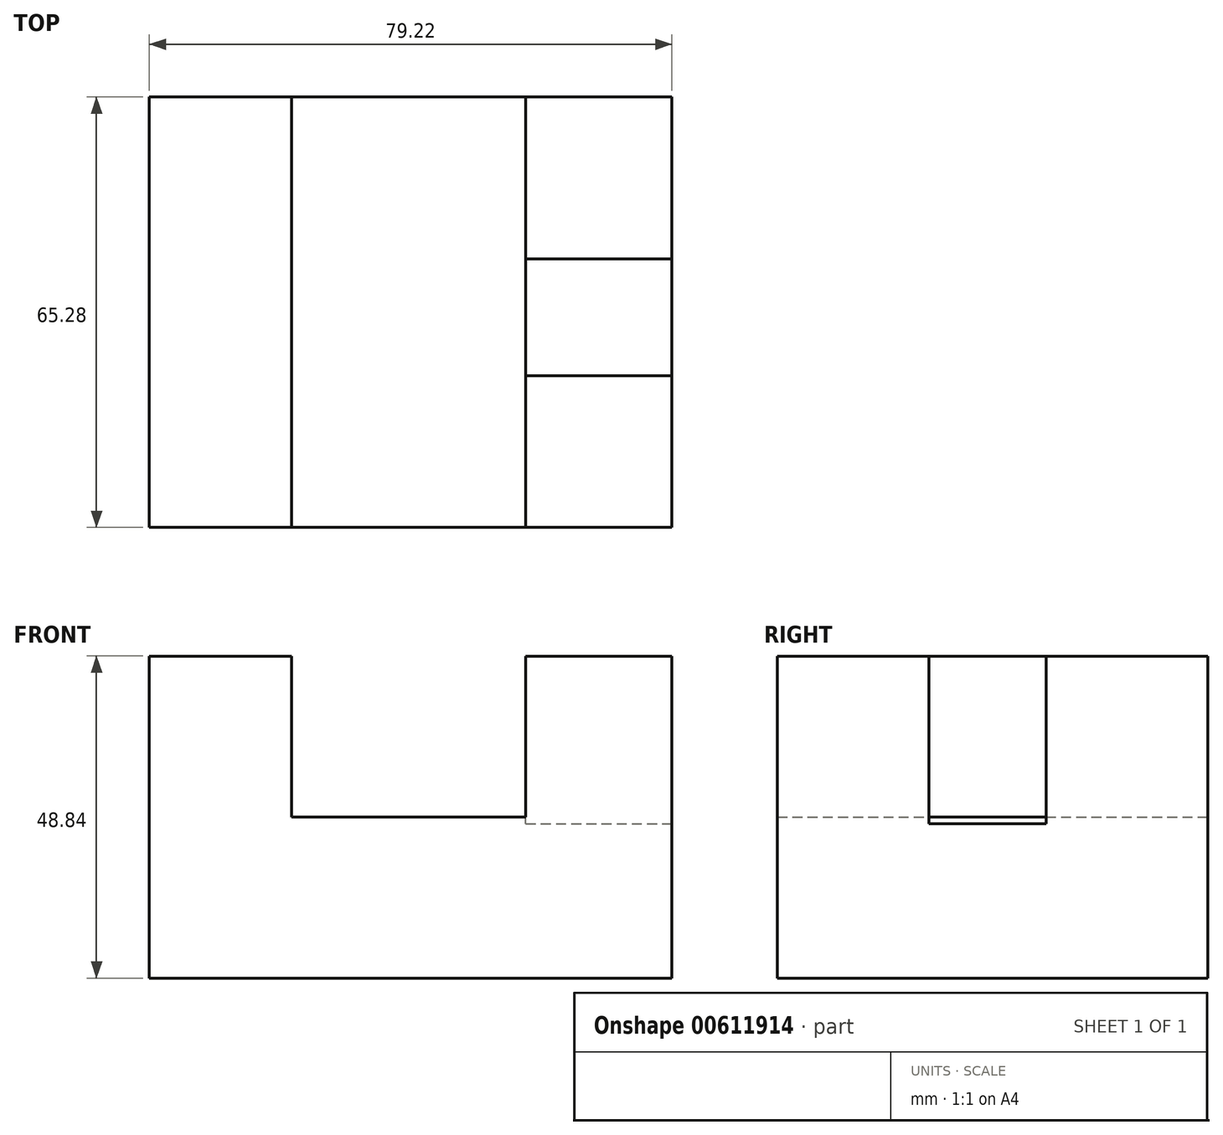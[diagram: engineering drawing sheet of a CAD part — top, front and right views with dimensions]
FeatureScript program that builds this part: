
annotation { "Feature Type Name" : "Feature", "Feature Type Description" : "" }
export const myFeature = defineFeature(function(context is Context, id is Id, definition is map)
    precondition{}
    {
        {
            var Q0;
            Q0=qCreatedBy(makeId("Front.planeOp"),FACE);
            var sketch = newSketch(context, id + "F0", { "sketchPlane" : qUnion([Q0])});
            skLineSegment(sketch, "E0.bottom", {"start": v(-39.6, 24.42) * mm, "end": v(-18.03, 24.42) * mm});
            skLineSegment(sketch, "E0.top", {"start": v(-39.6, -24.42) * mm, "end": v(39.6, -24.42) * mm});
            skLineSegment(sketch, "E0.left", {"start": v(-39.6, 24.42) * mm, "end": v(-39.6, -24.42) * mm});
            skLineSegment(sketch, "E0.right", {"start": v(39.6, 24.42) * mm, "end": v(39.6, -24.42) * mm});
            skPoint(sketch, "E0.middle", {"position": v(0, 0) * mm});
            skLineSegment(sketch, "E1", {"start": v(-18.03, 24.42) * mm, "end": v(-18.03, 0) * mm});
            skLineSegment(sketch, "E2", {"start": v(17.46, 24.42) * mm, "end": v(17.46, 0) * mm});
            skLineSegment(sketch, "E3", {"start": v(17.46, 0) * mm, "end": v(-11.22, 0) * mm});
            skLineSegment(sketch, "E4", {"start": v(-11.22, 0) * mm, "end": v(-18.03, 0) * mm});
            skLineSegment(sketch, "E5.trimOffspring", {"start": v(17.46, 24.42) * mm, "end": v(39.6, 24.42) * mm});
            skSolve(sketch);
        }
        {
            var Q0;
            Q0 = qSketchRegion(id + "F0", true);
            extrude(context, id + "F1", {"entities" : qUnion([Q0]), "depth" : 65.28 * mm, "offsetDistance" : 25.4 * mm});
        }
        {
            var Q0;
            Q0=makeQuery(id+"F1.opExtrude","SWEPT_FACE",FACE,{"disambiguationData":[OSD([sQuery(id+"F0.wireOp",EDGE,"E5.trimOffspring")])]});
            var sketch = newSketch(context, id + "F2", { "sketchPlane" : qUnion([Q0])});
            skLineSegment(sketch, "E6.bottom", {"start": v(17.46, -24.54) * mm, "end": v(39.6, -24.54) * mm});
            skLineSegment(sketch, "E6.top", {"start": v(17.46, -42.29) * mm, "end": v(39.6, -42.29) * mm});
            skLineSegment(sketch, "E6.left", {"start": v(17.46, -24.54) * mm, "end": v(17.46, -42.29) * mm});
            skLineSegment(sketch, "E6.right", {"start": v(39.6, -24.54) * mm, "end": v(39.6, -42.29) * mm});
            skSolve(sketch);
        }
        {
            var Q0;
            Q0=makeQuery(id+"F2.imprint","IMPRINT",FACE,{"disambiguationData":[TD([[makeQuery(id+"F2.imprint","IMPRINT",EDGE,{"derivedFrom":sQuery(id+"F2.wireOp",EDGE,"E6.bottom")}),-1.0]])]});
            extrude(context, id + "F3", {"entities" : qUnion([Q0]), "operationType" : NewBodyOperationType.REMOVE, "oppositeDirection" : true, "depth" : 25.4 * mm, "offsetDistance" : 25.4 * mm});
        }
    });
